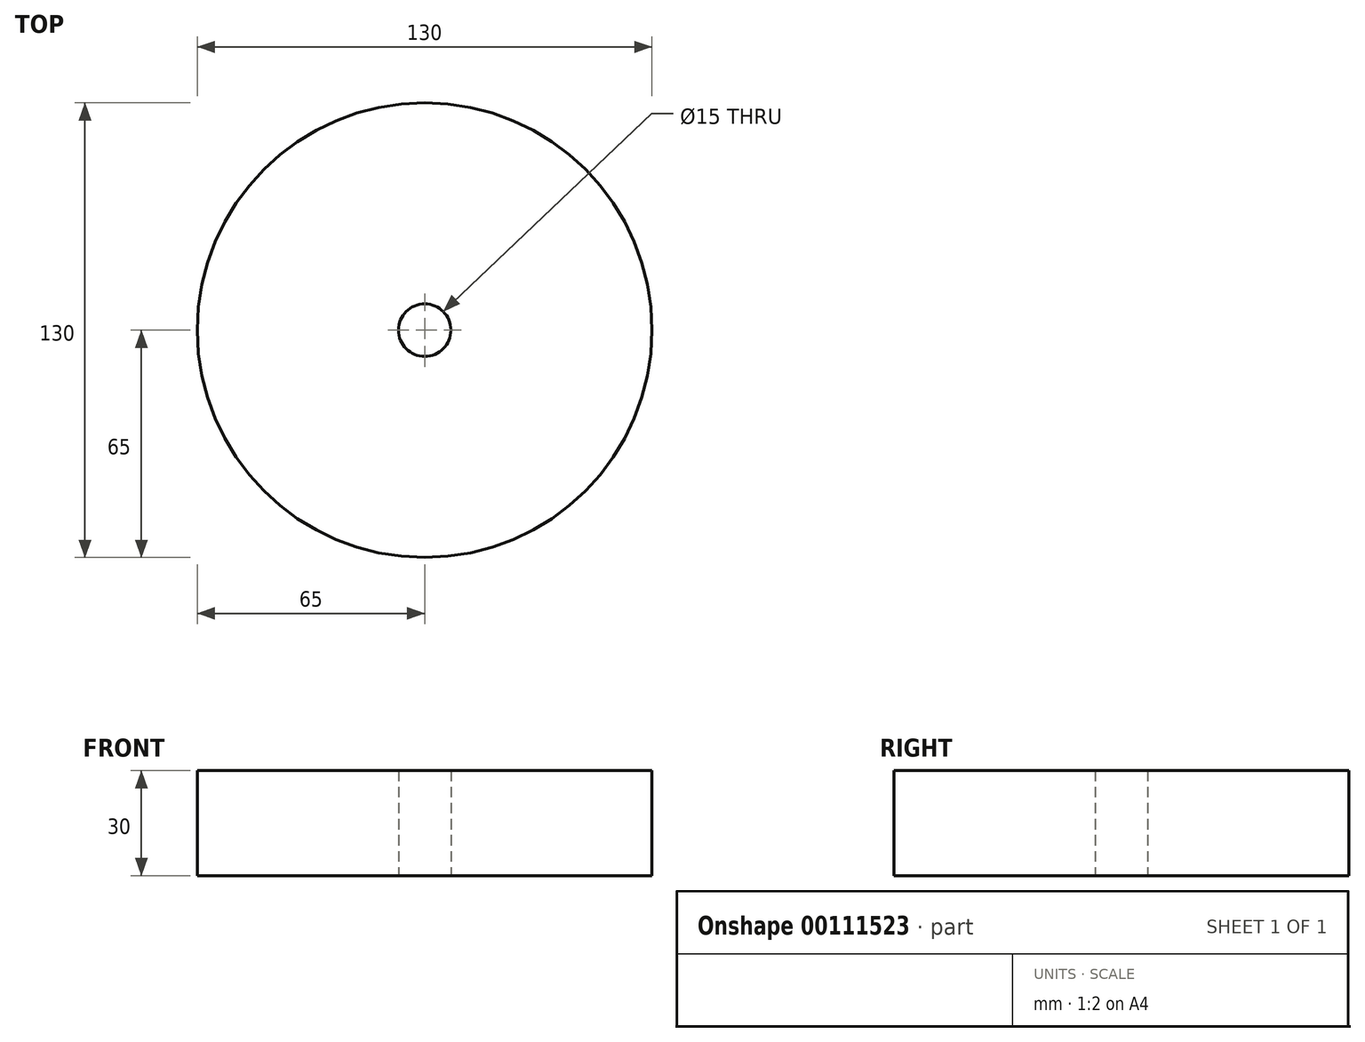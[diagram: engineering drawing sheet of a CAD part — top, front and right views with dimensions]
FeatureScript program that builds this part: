
annotation { "Feature Type Name" : "Feature", "Feature Type Description" : "" }
export const myFeature = defineFeature(function(context is Context, id is Id, definition is map)
    precondition{}
    {
        {
            var Q0;
            Q0=qCreatedBy(makeId("Top.planeOp"),FACE);
            var sketch = newSketch(context, id + "F0", { "sketchPlane" : qUnion([Q0])});
            skCircle(sketch, "E0", {"center": v(0, 0) * mm, "radius": 65 * mm});
            skCircle(sketch, "E1", {"center": v(0, 0) * mm, "radius": 7.5 * mm});
            skSolve(sketch);
        }
        {
            var Q0;
            Q0 = qSketchRegion(id + "F0", true);
            extrude(context, id + "F1", {"entities" : qUnion([Q0]), "endBound" : BoundingType.SYMMETRIC, "depth" : 30 * mm});
        }
    });
